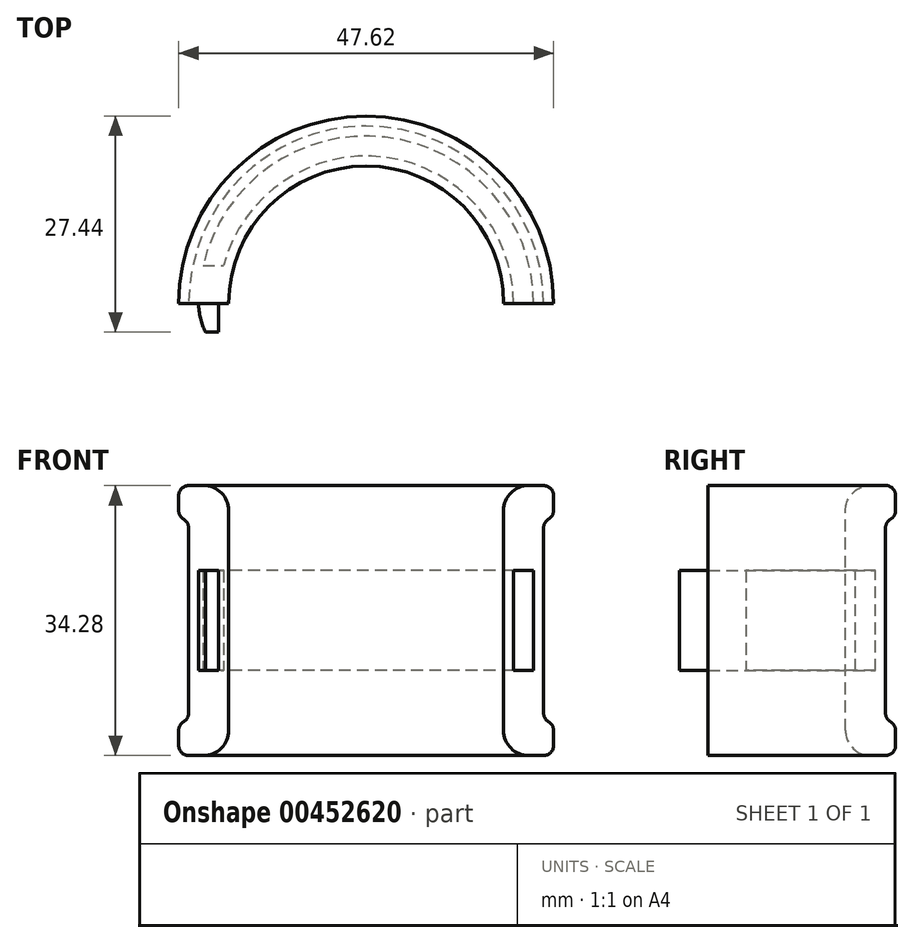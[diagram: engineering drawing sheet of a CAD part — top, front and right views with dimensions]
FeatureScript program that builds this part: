
annotation { "Feature Type Name" : "Feature", "Feature Type Description" : "" }
export const myFeature = defineFeature(function(context is Context, id is Id, definition is map)
    precondition{}
    {
        {
            var Q0;
            Q0=qCreatedBy(makeId("Front.planeOp"),FACE);
            var sketch = newSketch(context, id + "F0", { "sketchPlane" : qUnion([Q0])});
            skLineSegment(sketch, "E0", {"start": v(0, 21.5) * mm, "end": v(0, -21.5) * mm, "construction": true});
            skLineSegment(sketch, "E1.left", {"start": v(-17.46, 13.97) * mm, "end": v(-17.46, -13.97) * mm});
            skArc(sketch, "E2", {"start": v(-22.54, -12.7) * mm, "mid": v(-23.44, -13.07) * mm, "end": v(-23.81, -13.97) * mm});
            skArc(sketch, "E3", {"start": v(-23.81, 13.97) * mm, "mid": v(-23.44, 13.07) * mm, "end": v(-22.54, 12.7) * mm});
            skLineSegment(sketch, "E4.trimOffspring", {"start": v(-22.54, 12.7) * mm, "end": v(-22.54, -12.7) * mm});
            skLineSegment(sketch, "E5.bottom", {"start": v(-18.73, -6.35) * mm, "end": v(-21.27, -6.35) * mm});
            skLineSegment(sketch, "E5.top", {"start": v(-18.73, 6.35) * mm, "end": v(-21.27, 6.35) * mm});
            skLineSegment(sketch, "E5.left", {"start": v(-18.73, -6.35) * mm, "end": v(-18.73, 6.35) * mm});
            skLineSegment(sketch, "E5.right", {"start": v(-21.27, -6.35) * mm, "end": v(-21.27, 6.35) * mm});
            skPoint(sketch, "E5.middle", {"position": v(-20, 0) * mm});
            skPoint(sketch, "E6", {"position": v(0, 0) * mm});
            skPoint(sketch, "E7", {"position": v(-17.46, 0) * mm});
            skArc(sketch, "E8", {"start": v(-17.46, 13.97) * mm, "mid": v(-18.4, 16.22) * mm, "end": v(-20.64, 17.15) * mm});
            skArc(sketch, "E9", {"start": v(-20.64, -17.14) * mm, "mid": v(-18.4, -16.22) * mm, "end": v(-17.46, -13.97) * mm});
            skLineSegment(sketch, "E10", {"start": v(-20.64, 17.15) * mm, "end": v(-23.81, 17.15) * mm});
            skLineSegment(sketch, "E11", {"start": v(-23.81, 17.15) * mm, "end": v(-23.81, 13.97) * mm});
            skLineSegment(sketch, "E12", {"start": v(-20.64, -17.14) * mm, "end": v(-23.81, -17.14) * mm});
            skLineSegment(sketch, "E13", {"start": v(-23.81, -17.14) * mm, "end": v(-23.81, -13.97) * mm});
            skSolve(sketch);
        }
        {
            var Q0;
            Q0=makeQuery(id+"F0.imprint","IMPRINT",FACE,{"disambiguationData":[TD([[makeQuery(id+"F0.imprint","IMPRINT",EDGE,{"derivedFrom":sQuery(id+"F0.wireOp",EDGE,"E1.left")}),-1.0]])]});
            var Q1;
            Q1=sQuery(id+"F0.wireOp",EDGE,"E0");
            revolve(context, id + "F1", {"entities" : qUnion([Q0]), "axis" : qUnion([Q1]), "revolveType" : RevolveType.ONE_DIRECTION, "angle" : 180 * degree});
        }
        {
            var Q0;
            Q0=qCreatedBy(makeId("Top.planeOp"),FACE);
            var sketch = newSketch(context, id + "F2", { "sketchPlane" : qUnion([Q0])});
            skArc(sketch, "E14.1", {"start": v(-20.72, 4.81) * mm, "mid": v(-21.13, 2.42) * mm, "end": v(-21.27, 0) * mm});
            skArc(sketch, "E14.2", {"start": v(-18.1, 4.81) * mm, "mid": v(-18.57, 2.43) * mm, "end": v(-18.73, 0) * mm});
            skArc(sketch, "E15", {"start": v(-21.27, 0) * mm, "mid": v(-21.05, -1.87) * mm, "end": v(-20.39, -3.63) * mm});
            skLineSegment(sketch, "E16", {"start": v(-20.39, -3.63) * mm, "end": v(-18.73, -3.63) * mm});
            skLineSegment(sketch, "E17", {"start": v(-20.72, 4.81) * mm, "end": v(-18.1, 4.81) * mm});
            skLineSegment(sketch, "E18", {"start": v(-18.73, 0) * mm, "end": v(-18.73, -3.63) * mm});
            skPoint(sketch, "E19.orphan", {"position": v(21.27, 0) * mm});
            skPoint(sketch, "E20.orphan", {"position": v(18.73, 0) * mm});
            skSolve(sketch);
        }
        {
            var Q0;
            Q0=makeQuery(id+"F2.imprint","IMPRINT",FACE,{"disambiguationData":[TD([[makeQuery(id+"F2.imprint","IMPRINT",EDGE,{"derivedFrom":sQuery(id+"F2.wireOp",EDGE,"E14.1")}),1.0]])]});
            extrude(context, id + "F3", {"entities" : qUnion([Q0]), "operationType" : NewBodyOperationType.ADD, "endBound" : BoundingType.SYMMETRIC, "depth" : 12.7 * mm});
        }
        {
            var Q0;
            Q0=makeQuery(id+"F1.opRevolve","SWEPT_EDGE",EDGE,{"disambiguationData":[OSD([sQuery(id+"F0.wireOp",EDGE,"E3"),sQuery(id+"F0.wireOp",EDGE,"E4.trimOffspring")])]});
            var Q1;
            Q1=makeQuery(id+"F1.opRevolve","SWEPT_EDGE",EDGE,{"disambiguationData":[OSD([sQuery(id+"F0.wireOp",EDGE,"E2"),sQuery(id+"F0.wireOp",EDGE,"E4.trimOffspring")])]});
            var Q2;
            Q2=makeQuery(id+"F1.opRevolve","SWEPT_EDGE",EDGE,{"disambiguationData":[OSD([sQuery(id+"F0.wireOp",EDGE,"E10"),sQuery(id+"F0.wireOp",EDGE,"E11")])]});
            var Q3;
            Q3=makeQuery(id+"F1.opRevolve","SWEPT_EDGE",EDGE,{"disambiguationData":[OSD([sQuery(id+"F0.wireOp",EDGE,"E12"),sQuery(id+"F0.wireOp",EDGE,"E13")])]});
            fillet(context, id + "F4", {"entities" : qUnion([Q0, Q1, Q2, Q3]), "radius" : 1.27 * mm, "tangentPropagation" : true, "allowEdgeOverflow" : false});
        }
    });
